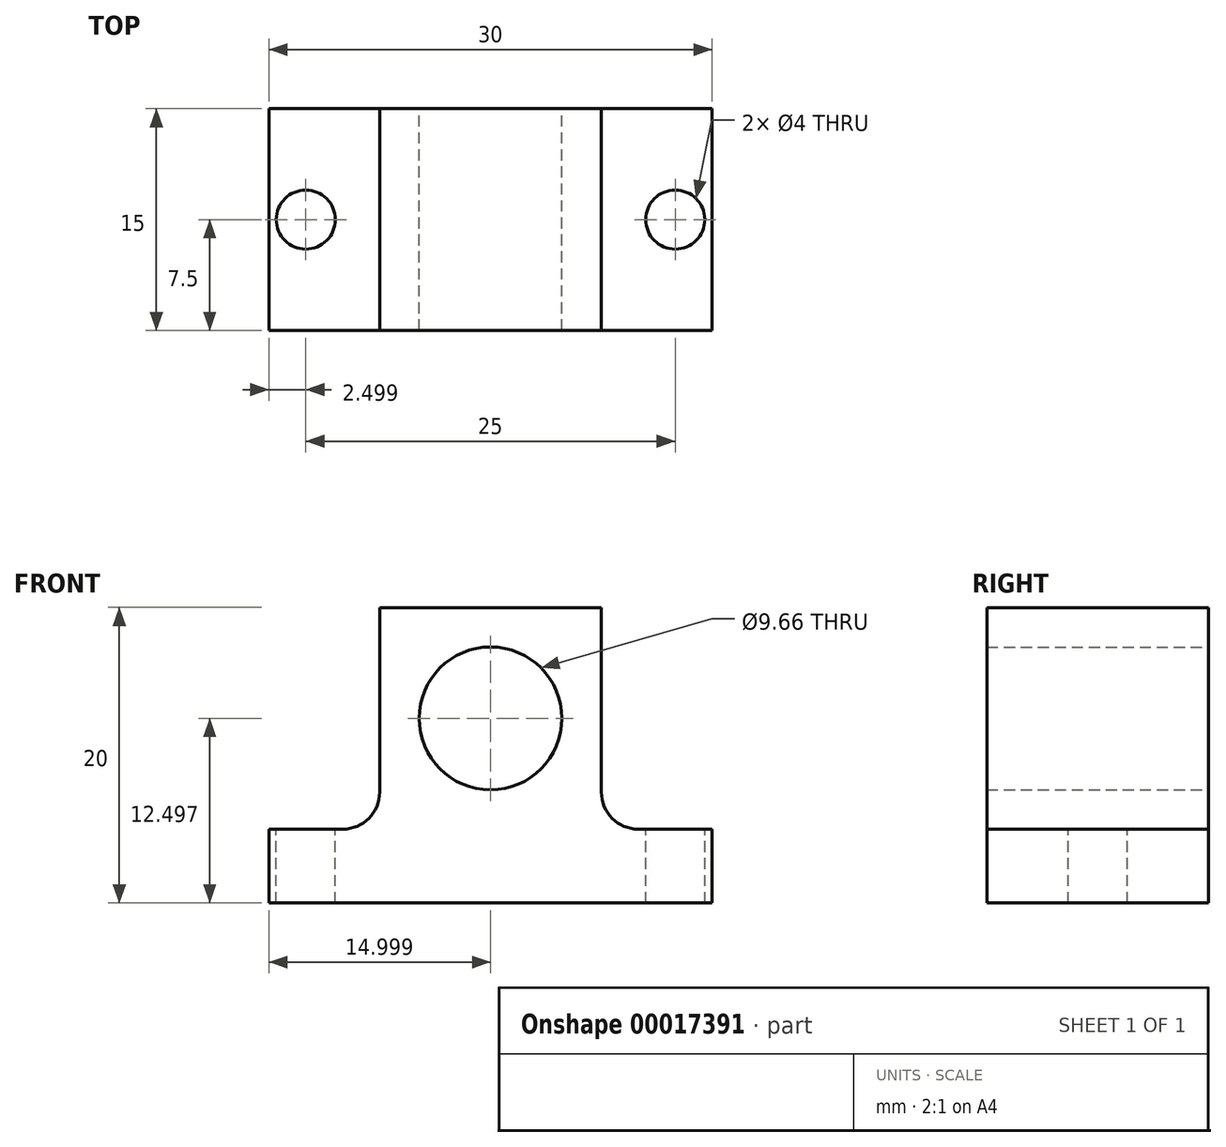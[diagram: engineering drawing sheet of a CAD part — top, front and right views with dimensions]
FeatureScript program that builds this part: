
annotation { "Feature Type Name" : "Feature", "Feature Type Description" : "" }
export const myFeature = defineFeature(function(context is Context, id is Id, definition is map)
    precondition{}
    {
        {
            var Q0;
            Q0=qCreatedBy(makeId("Front.planeOp"),FACE);
            var sketch = newSketch(context, id + "F0", { "sketchPlane" : qUnion([Q0])});
            skLineSegment(sketch, "E0", {"start": v(-17.05, 10.16) * mm, "end": v(-22.05, 10.16) * mm});
            skLineSegment(sketch, "E1", {"start": v(-22.05, 10.16) * mm, "end": v(-22.05, 5.16) * mm});
            skLineSegment(sketch, "E2", {"start": v(-22.05, 5.16) * mm, "end": v(7.95, 5.16) * mm});
            skLineSegment(sketch, "E3", {"start": v(7.95, 5.16) * mm, "end": v(7.95, 10.16) * mm});
            skLineSegment(sketch, "E4", {"start": v(7.95, 10.16) * mm, "end": v(2.95, 10.16) * mm});
            skLineSegment(sketch, "E5", {"start": v(0.45, 12.66) * mm, "end": v(0.45, 25.16) * mm});
            skLineSegment(sketch, "E6", {"start": v(0.45, 25.16) * mm, "end": v(-14.55, 25.16) * mm});
            skLineSegment(sketch, "E7", {"start": v(-14.55, 25.16) * mm, "end": v(-14.55, 12.66) * mm});
            skCircle(sketch, "E8", {"center": v(-7.05, 17.66) * mm, "radius": 4.83 * mm});
            skPoint(sketch, "E9.visualSharp", {"position": v(0.45, 10.16) * mm});
            skArc(sketch, "E9.filletArc", {"start": v(0.45, 12.66) * mm, "mid": v(1.18, 10.89) * mm, "end": v(2.95, 10.16) * mm});
            skPoint(sketch, "E10.visualSharp", {"position": v(-14.55, 10.16) * mm});
            skArc(sketch, "E10.filletArc", {"start": v(-17.05, 10.16) * mm, "mid": v(-15.28, 10.89) * mm, "end": v(-14.55, 12.66) * mm});
            skSolve(sketch);
        }
        {
            var Q0;
            Q0=makeQuery(id+"F0.imprint","IMPRINT",FACE,{"disambiguationData":[TD([[makeQuery(id+"F0.imprint","IMPRINT",EDGE,{"derivedFrom":sQuery(id+"F0.wireOp",EDGE,"E0")}),1.0]])]});
            extrude(context, id + "F1", {"entities" : qUnion([Q0]), "depth" : 15 * mm});
        }
        {
            var Q0;
            Q0=makeQuery(id+"F1.opExtrude","SWEPT_FACE",FACE,{"disambiguationData":[OSD([sQuery(id+"F0.wireOp",EDGE,"E0")])]});
            var sketch = newSketch(context, id + "F2", { "sketchPlane" : qUnion([Q0])});
            skLineSegment(sketch, "E11", {"start": v(-22.05, -7.5) * mm, "end": v(-17.05, -7.5) * mm});
            skCircle(sketch, "E12", {"center": v(-19.55, -7.5) * mm, "radius": 2 * mm});
            skSolve(sketch);
        }
        {
            var Q0;
            Q0=makeQuery(id+"F1.opExtrude","SWEPT_FACE",FACE,{"disambiguationData":[OSD([sQuery(id+"F0.wireOp",EDGE,"E4")])]});
            var sketch = newSketch(context, id + "F3", { "sketchPlane" : qUnion([Q0])});
            skLineSegment(sketch, "E13", {"start": v(2.95, -7.5) * mm, "end": v(7.95, -7.5) * mm});
            skCircle(sketch, "E14", {"center": v(5.45, -7.5) * mm, "radius": 2 * mm});
            skSolve(sketch);
        }
        {
            var Q0;
            Q0 = qSketchRegion(id + "F3", true);
            extrude(context, id + "F4", {"entities" : qUnion([Q0]), "operationType" : NewBodyOperationType.REMOVE, "endBound" : BoundingType.THROUGH_ALL, "oppositeDirection" : true, "depth" : 25 * mm});
        }
        {
            var Q0;
            {var subQ0=sQuery(id+"F2.wireOp",EDGE,"E12");var subQ1=sQuery(id+"F2.wireOp",EDGE,"E11");var subQ3=makeQuery(id+"F2.imprint","INTERSECT",VERTEX,{"disambiguationData":[OD(0.0)],"derivedFrom":[subQ1,subQ0]});Q0=makeQuery(id+"F2.imprint","IMPRINT",FACE,{"disambiguationData":[TD([[makeQuery(id+"F2.imprint","IMPRINT",EDGE,{"disambiguationData":[TD([[subQ3,-1.0]])],"derivedFrom":subQ1}),-1.0]])]});}
            var Q1;
            {var subQ0=sQuery(id+"F2.wireOp",EDGE,"E12");var subQ1=sQuery(id+"F2.wireOp",EDGE,"E11");var subQ3=makeQuery(id+"F2.imprint","INTERSECT",VERTEX,{"disambiguationData":[OD(0.0)],"derivedFrom":[subQ1,subQ0]});Q1=makeQuery(id+"F2.imprint","IMPRINT",FACE,{"disambiguationData":[TD([[makeQuery(id+"F2.imprint","IMPRINT",EDGE,{"disambiguationData":[TD([[subQ3,-1.0]])],"derivedFrom":subQ1}),1.0]])]});}
            extrude(context, id + "F5", {"entities" : qUnion([Q0, Q1]), "operationType" : NewBodyOperationType.REMOVE, "oppositeDirection" : true, "depth" : 25 * mm});
        }
    });
